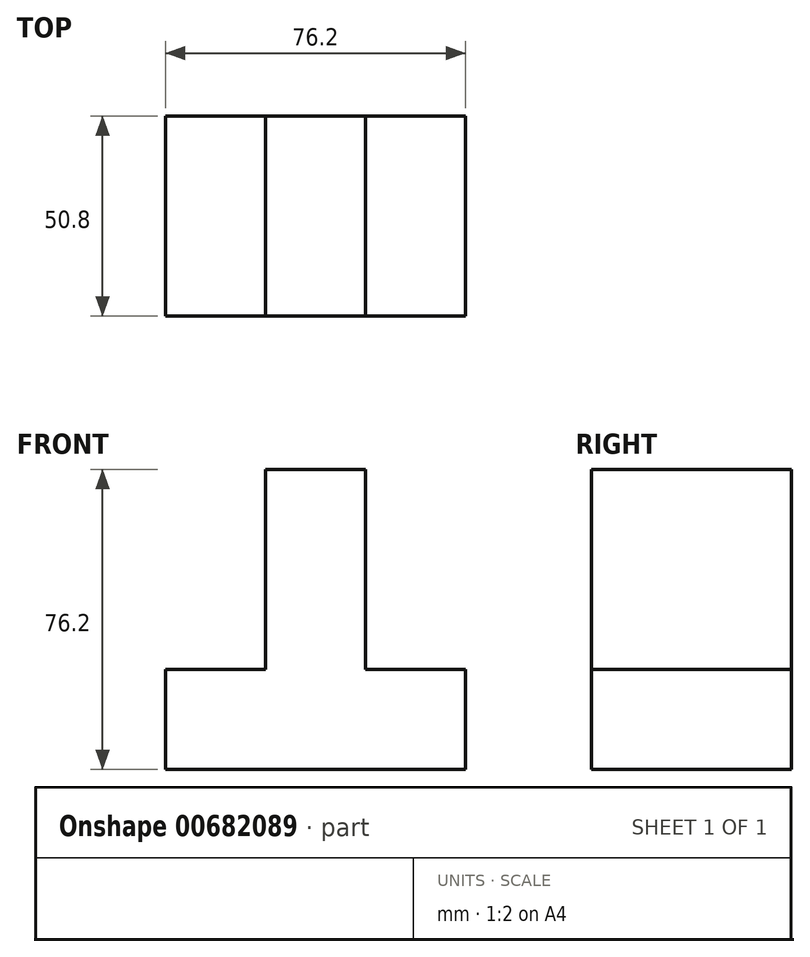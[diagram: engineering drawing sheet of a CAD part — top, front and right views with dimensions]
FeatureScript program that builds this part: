
annotation { "Feature Type Name" : "Feature", "Feature Type Description" : "" }
export const myFeature = defineFeature(function(context is Context, id is Id, definition is map)
    precondition{}
    {
        {
            var Q0;
            Q0=qCreatedBy(makeId("Front.planeOp"),FACE);
            var sketch = newSketch(context, id + "F0", { "sketchPlane" : qUnion([Q0])});
            skLineSegment(sketch, "E0", {"start": v(0, 0) * mm, "end": v(-76.2, 0) * mm});
            skLineSegment(sketch, "E1", {"start": v(-76.2, 0) * mm, "end": v(-76.2, 25.4) * mm});
            skLineSegment(sketch, "E2", {"start": v(-76.2, 25.4) * mm, "end": v(-50.8, 25.4) * mm});
            skLineSegment(sketch, "E3", {"start": v(-50.8, 25.4) * mm, "end": v(-50.8, 76.2) * mm});
            skLineSegment(sketch, "E4", {"start": v(-50.8, 76.2) * mm, "end": v(-25.4, 76.2) * mm});
            skLineSegment(sketch, "E5", {"start": v(-25.4, 76.2) * mm, "end": v(-25.4, 25.4) * mm});
            skLineSegment(sketch, "E6", {"start": v(-25.4, 25.4) * mm, "end": v(0, 25.4) * mm});
            skLineSegment(sketch, "E7", {"start": v(0, 25.4) * mm, "end": v(0, 0) * mm});
            skSolve(sketch);
        }
        {
            var Q0;
            Q0 = qSketchRegion(id + "F0", true);
            extrude(context, id + "F1", {"entities" : qUnion([Q0]), "depth" : 50.8 * mm, "offsetDistance" : 25.4 * mm});
        }
    });
